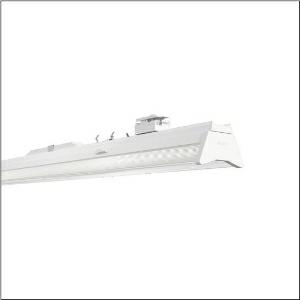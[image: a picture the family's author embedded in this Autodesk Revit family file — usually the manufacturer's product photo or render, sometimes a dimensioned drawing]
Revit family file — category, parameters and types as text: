
# Revit family: licross_r__21_performance_mo_52td16vn455g_74b2
name_source: partatom
category: Lighting Fixtures
units: mm (PartAtom-declared; Revit-internal decimal feet)

## family parameters
Cut with Voids When Loaded = No
Host = Face
Light Source = No
Part Type = Normal
Room Calculation Point = No
Round Connector Dimension = Use Diameter
Shared = No

## types (1)
- --- (1 x LED, 5500 lm, 30 W, 4000K)
    Apparent Load = 30 VA
    CIE Flux Codes = 66 88 96 79 100
    Color Rendering = 80
    Color Temperature = 4000K
    Default Elevation = 1800 mm
    Description = Licross® 21 Performance MO, luminaire insert, of sheet steel, galvanised, coil coated, white, length: 1.500mm, width: 120mm, height: 123mm, LED rated luminous flux: 5.500lm, light colour: 840, control gear: DALI 2, CLO, with plug, 5-pole, with phase selection, mains connection: 220..240V, AC, 50/60Hz, start of lifetime: 30W, end of service life: 36W, halogen-free wiring, primary light control with lens, of plastic, primary optical cover: cover, of PMMA, light emission: direct/indirect distribution, primary light characteristic: symmetric, protection rating (complete): IP54, insulation class (complete): insulation class I (protective earthing), certification: CE, ENEC, VDE, UKCA, protection symbol: D if used in an environment with non-conductive dust loads with corresponding accessories, impact resistance: IK06, permissible ambient temperature for indoor applications: -25..+50°C, corresponds to IFS (International Featured Standards) requirements for safety and quality in the food industry, reducing of maximum allowable ambient temperature of 5°C with ceiling mounting, LABS conformity tested according to VDMA 24364:2018-05, packaging unit: 1 piece
    Height = 114 mm
    Lamp = 1 x LED
    Lamp Light Flux = 5500 lm
    Lamp Power = 30 W
    Lamp count = 1
    Length = 1500 mm
    Luminous efficacy = 183 lm/W
    Manufacturer = Siteco
    ModVariant = No
    Model = 52TD16VN455G
    Mounting Place = Ceiling
    Mounting Type = Pendant
    Number of Poles = 1
    OnlyDefault = Yes
    Power Factor = 1
    Product Name = Licross® 21 Performance MO
    Product group = luminaire insert
    ProductGroupID = 902
    Protection Class = Protection class I
    Protection Degree = IP 54
    RLX_Detail_Level = 1
    RLX_Emergency_Light_Flux = 0 lm
    RLX_Emergency_Type = 0
    RLX_Emergency_Type_DB = No
    RlxData = <blob elided: 33493 chars, md5=17ffc177>
    Socket = socket
    Standby Power = 0 W
    System Light Flux = 5500 lm
    System Power = 30 W
    Type Comments = factory setting: luminous flux: 100 % | dim-lin: 254 | 203 mA
    Type Image = l_1256138.jpg
    URL = http://relux.com
    VarID = @adj_082948
    Voltage = 0 V
    Weight = 0.00 kg
    Width = 120 mm

## geometry (parser evidence)
native form markers: Blend x4, Sweep x11
no freeform markers — native parametric forms only
